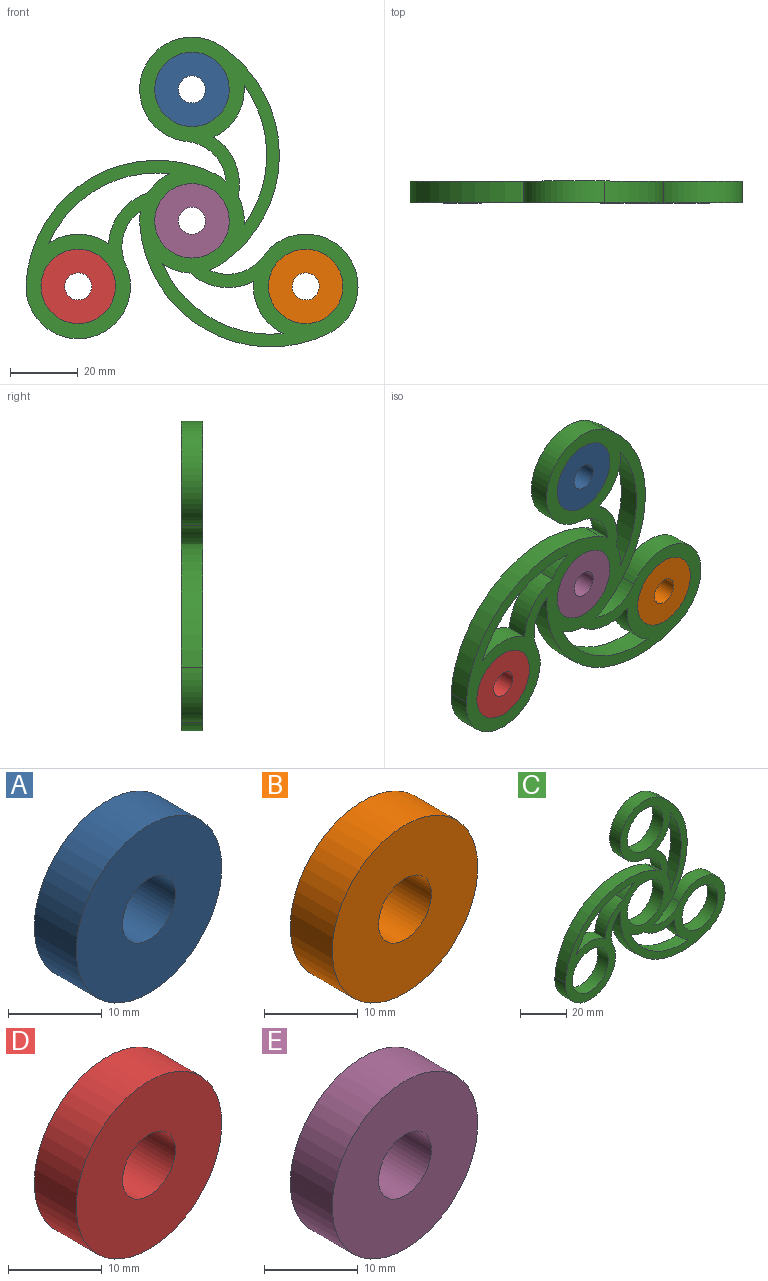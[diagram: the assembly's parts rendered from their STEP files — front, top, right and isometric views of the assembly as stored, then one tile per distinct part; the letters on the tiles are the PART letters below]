
ASSEMBLY  parts=5 mates=4
PART A: 4 faces, bbox 22x6.4x22 mm
  f0: cylinder r=4mm len=8mm, axis (0,1,0), area 159.6mm2, adj f2,f3
  f1: cylinder r=11mm len=22mm, axis (0,1,0), area 438.9mm2, adj f2,f3
  f2: plane 22x22mm, normal (0,-1,0), area 329.9mm2, adj f0,f1
  f3: plane 22x22mm, normal (0,1,0), area 329.9mm2, adj f0,f1
PART B: 4 faces, bbox 22x6.4x22 mm
  f0: cylinder r=4mm len=8mm, axis (0,1,0), area 159.6mm2, adj f2,f3
  f1: cylinder r=11mm len=22mm, axis (0,1,0), area 438.9mm2, adj f2,f3
  f2: plane 22x22mm, normal (0,-1,0), area 329.9mm2, adj f0,f1
  f3: plane 22x22mm, normal (0,1,0), area 329.9mm2, adj f0,f1
PART C: 30 faces, bbox 98.1x6.4x91.5 mm
  f0: cylinder r=15.45mm len=6.35mm, axis (0,1,0), area 24.4mm2, adj f14,f15,f22,f23
  f1: cylinder r=15.45mm len=8.12mm, axis (0,1,0), area 55mm2, adj f14,f15,f20,f21
  f2: cylinder r=15.45mm len=6.35mm, axis (0,1,0), area 24.4mm2, adj f4,f14,f15,f24
  f3: cylinder r=15.45mm len=6.38mm, axis (0,1,0), area 55mm2, adj f14,f15,f25,f27
  f4: cylinder r=12.75mm len=11.68mm, axis (0,1,0), area 113.1mm2, adj f2,f13,f14,f15
  f5: cylinder r=15.45mm len=6.35mm, axis (0,1,0), area 24.4mm2, adj f6,f14,f15,f19
  f6: cylinder r=38.76mm len=64.49mm, axis (0,1,0), area 483.7mm2, adj f5,f13,f14,f15
  f7: cylinder r=16.71mm len=17.54mm, axis (0,1,0), area 128.2mm2, adj f8,f12,f14,f15
  f8: cylinder r=15.45mm len=15.22mm, axis (0,1,0), area 119.5mm2, adj f7,f9,f14,f15
  f9: cylinder r=35.01mm len=41.13mm, axis (0,1,0), area 279.2mm2, adj f8,f12,f14,f15
  f10: cylinder r=11mm len=22mm, axis (0,1,0), area 438.9mm2, adj f14,f15
  f11: cylinder r=11mm len=22mm, axis (0,1,0), area 438.9mm2, adj f14,f15
  f12: cylinder r=15.45mm len=8.37mm, axis (0,1,0), area 55mm2, adj f7,f9,f14,f15
  f13: cylinder r=15.45mm len=30.82mm, axis (0,1,0), area 356.5mm2, adj f4,f6,f14,f15
  f14: plane 98.07x91.49mm, normal (0,-1,0), area 2306.1mm2, adj f0,f1,f2,f3,f4,f5,f6,f7
  f15: plane 98.07x91.49mm, normal (0,1,0), area 2306.1mm2, adj f0,f1,f2,f3,f4,f5,f6,f7
  f16: cylinder r=15.45mm len=29.29mm, axis (0,1,0), area 356.5mm2, adj f14,f15,f19,f22
  f17: cylinder r=15.45mm len=15.39mm, axis (0,1,0), area 119.5mm2, adj f14,f15,f20,f21
  f18: cylinder r=11mm len=22mm, axis (0,1,0), area 438.9mm2, adj f14,f15
  f19: cylinder r=12.75mm len=15.87mm, axis (0,1,0), area 113.1mm2, adj f5,f14,f15,f16
  f20: cylinder r=35.01mm len=35.62mm, axis (0,1,0), area 279.2mm2, adj f1,f14,f15,f17
  f21: cylinder r=16.71mm len=18.81mm, axis (0,1,0), area 128.2mm2, adj f1,f14,f15,f17
  f22: cylinder r=38.76mm len=55.85mm, axis (0,1,0), area 483.7mm2, adj f0,f14,f15,f16
  f23: cylinder r=12.75mm len=15.8mm, axis (0,1,0), area 113.1mm2, adj f0,f14,f15,f29
  f24: cylinder r=38.76mm len=55.85mm, axis (0,1,0), area 483.7mm2, adj f2,f14,f15,f29
  f25: cylinder r=16.71mm len=15.05mm, axis (0,1,0), area 128.2mm2, adj f3,f14,f15,f26
  f26: cylinder r=15.45mm len=17.68mm, axis (0,1,0), area 119.5mm2, adj f14,f15,f25,f27
  f27: cylinder r=35.01mm len=35.62mm, axis (0,1,0), area 279.2mm2, adj f3,f14,f15,f26
  f28: cylinder r=11mm len=22mm, axis (0,1,0), area 438.9mm2, adj f14,f15
  f29: cylinder r=15.45mm len=30.89mm, axis (0,1,0), area 356.5mm2, adj f14,f15,f23,f24
PART D: 4 faces, bbox 22x6.4x22 mm
  f0: cylinder r=4mm len=8mm, axis (0,1,0), area 159.6mm2, adj f2,f3
  f1: cylinder r=11mm len=22mm, axis (0,1,0), area 438.9mm2, adj f2,f3
  f2: plane 22x22mm, normal (0,-1,0), area 329.9mm2, adj f0,f1
  f3: plane 22x22mm, normal (0,1,0), area 329.9mm2, adj f0,f1
PART E: 4 faces, bbox 22x6.4x22 mm
  f0: cylinder r=4mm len=8mm, axis (0,1,0), area 159.6mm2, adj f2,f3
  f1: cylinder r=11mm len=22mm, axis (0,1,0), area 438.9mm2, adj f2,f3
  f2: plane 22x22mm, normal (0,-1,0), area 329.9mm2, adj f0,f1
  f3: plane 22x22mm, normal (0,1,0), area 329.9mm2, adj f0,f1
PLACE A t=(21.69,7.99,-27.89)mm
PLACE B t=(90.37,7.99,-26.76)mm
PLACE C t=(-0.41,7.99,-1.4)mm
PLACE D t=(-34.01,7.99,-20.79)mm
PLACE E t=(47.37,7.99,-44.62)mm
MATE fastened A.f0 <-> C.f8  axis (0,1,0) through (-0.41,7.99,37.39)mm
MATE fastened D.f1 <-> C.f26  axis (0,1,0) through (-34.01,7.99,-20.79)mm
MATE fastened E.f0 <-> C.f10  axis (0,1,0) through (-0.41,7.99,-1.4)mm
MATE fastened B.f0 <-> C.f16  axis (0,1,0) through (33.18,7.99,-20.79)mm
